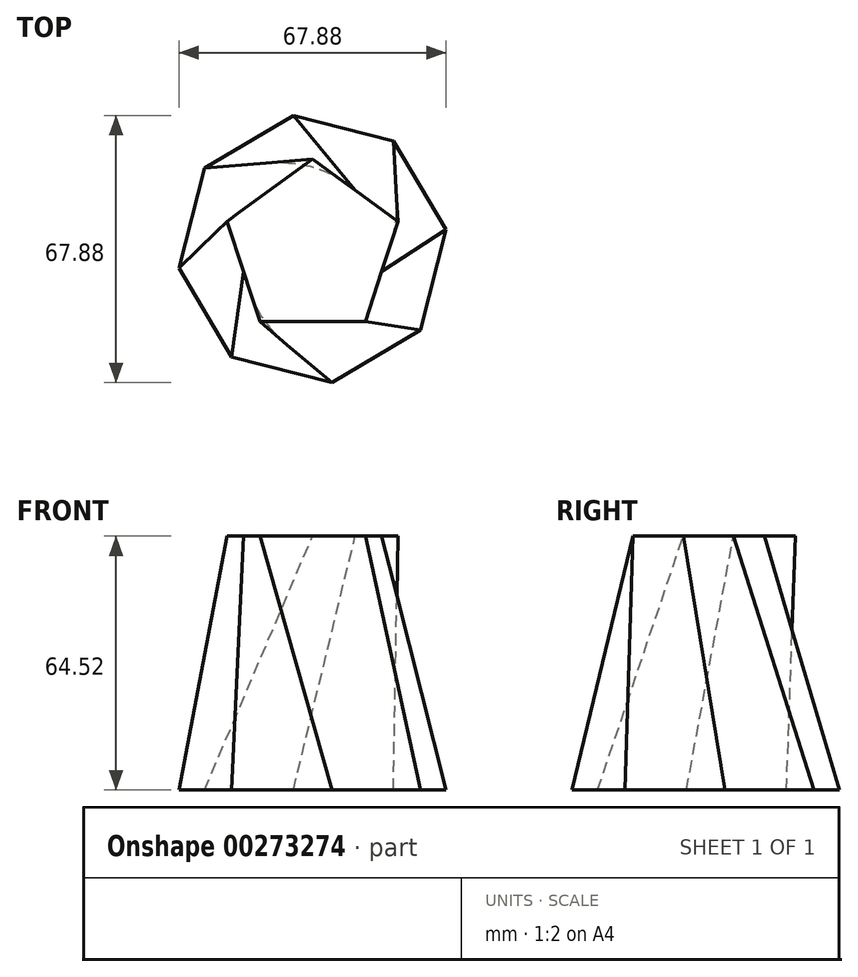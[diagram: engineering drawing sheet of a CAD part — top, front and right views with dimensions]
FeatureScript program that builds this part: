
annotation { "Feature Type Name" : "Feature", "Feature Type Description" : "" }
export const myFeature = defineFeature(function(context is Context, id is Id, definition is map)
    precondition{}
    {
        {
            var Q0;
            Q0=qCreatedBy(makeId("Top.planeOp"),FACE);
            var sketch = newSketch(context, id + "F0", { "sketchPlane" : qUnion([Q0])});
            skCircle(sketch, "E0.cCircle", {"center": v(0, 0) * mm, "radius": 31.68 * mm, "construction": true});
            skLineSegment(sketch, "E0.0", {"start": v(20.54, 27.45) * mm, "end": v(33.94, 4.9) * mm});
            skLineSegment(sketch, "E0.1", {"start": v(33.94, 4.9) * mm, "end": v(27.45, -20.54) * mm});
            skLineSegment(sketch, "E0.2", {"start": v(27.45, -20.54) * mm, "end": v(4.9, -33.94) * mm});
            skLineSegment(sketch, "E0.3", {"start": v(4.9, -33.94) * mm, "end": v(-20.54, -27.45) * mm});
            skLineSegment(sketch, "E0.4", {"start": v(-20.54, -27.45) * mm, "end": v(-33.94, -4.9) * mm});
            skLineSegment(sketch, "E0.5", {"start": v(-33.94, -4.9) * mm, "end": v(-27.45, 20.54) * mm});
            skLineSegment(sketch, "E0.6", {"start": v(-27.45, 20.54) * mm, "end": v(-4.9, 33.94) * mm});
            skLineSegment(sketch, "E0.7", {"start": v(-4.9, 33.94) * mm, "end": v(20.54, 27.45) * mm});
            skPoint(sketch, "E0.0.midPoint", {"position": v(27.24, 16.17) * mm});
            skSolve(sketch);
        }
        {
            var Q0;
            Q0=qCreatedBy(makeId("Top.planeOp"),FACE);
            cPlane(context, id + "F1", {"entities" : qUnion([Q0]), "cplaneType" : CPlaneType.OFFSET, "offset" : 64.52 * mm, "width" : 152.4 * mm, "height" : 152.4 * mm});
        }
        {
            var Q0;
            Q0=qCreatedBy(id+"F1.planeOp",FACE);
            var sketch = newSketch(context, id + "F2", { "sketchPlane" : qUnion([Q0])});
            skCircle(sketch, "E1.cCircle", {"center": v(0, 0) * mm, "radius": 18.44 * mm, "construction": true});
            skLineSegment(sketch, "E1.0", {"start": v(13.4, -18.44) * mm, "end": v(-13.4, -18.44) * mm});
            skLineSegment(sketch, "E1.1", {"start": v(-13.4, -18.44) * mm, "end": v(-21.68, 7.04) * mm});
            skLineSegment(sketch, "E1.2", {"start": v(-21.68, 7.04) * mm, "end": v(0, 22.8) * mm});
            skLineSegment(sketch, "E1.3", {"start": v(0, 22.8) * mm, "end": v(21.68, 7.04) * mm});
            skLineSegment(sketch, "E1.4", {"start": v(21.68, 7.04) * mm, "end": v(13.4, -18.44) * mm});
            skPoint(sketch, "E1.0.midPoint", {"position": v(0, -18.44) * mm});
            skSolve(sketch);
        }
        {
            var Q0;
            Q0=makeQuery(id+"F0.imprint","IMPRINT",FACE,{"disambiguationData":[TD([[makeQuery(id+"F0.imprint","IMPRINT",EDGE,{"derivedFrom":sQuery(id+"F0.wireOp",EDGE,"E0.0")}),-1.0]])]});
            var Q1;
            Q1=makeQuery(id+"F2.imprint","IMPRINT",FACE,{"disambiguationData":[TD([[makeQuery(id+"F2.imprint","IMPRINT",EDGE,{"derivedFrom":sQuery(id+"F2.wireOp",EDGE,"E1.0")}),-1.0]])]});
            loft(context, id + "F3", {"sheetProfilesArray" : [{ "sheetProfileEntities" : qUnion([Q0]) }, { "sheetProfileEntities" : qUnion([Q1]) }]});
        }
    });
